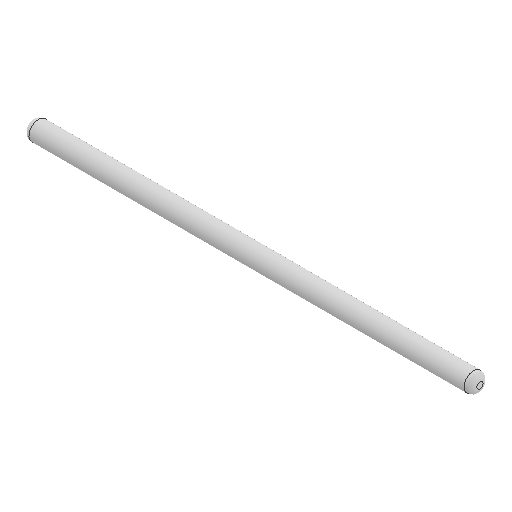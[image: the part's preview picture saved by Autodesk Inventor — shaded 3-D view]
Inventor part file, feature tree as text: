
AUTODESK INVENTOR PART (.ipt)
format: ipt  version: 2022 (Build 260153000, 153)  size: 89,600 bytes
history: native  units: mm
features: other x1, extrude x1, fillet x1, sketch x1
ambient origin geometry x8: Origin, YZ Plane, XZ Plane, XY Plane, X Axis, Y Axis, Z Axis, Center Point
bodies: Body1 (feature_tree)
feature tree (4):
  other  "Твердое тело1"
  extrude  "Выдавливание1"  Depth=3.0mm
  fillet  "Сопряжение1"  Radius=70.0mm
  sketch  "Эскиз1"
